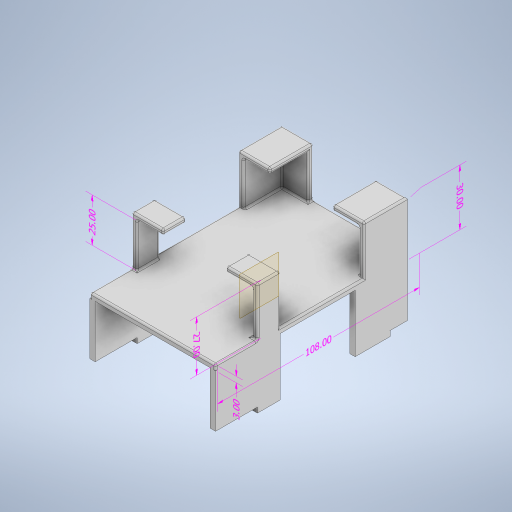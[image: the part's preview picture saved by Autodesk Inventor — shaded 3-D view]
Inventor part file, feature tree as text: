
AUTODESK INVENTOR PART (.ipt)
format: ipt  version: 2023 (Build 270158000, 158)  size: 560,128 bytes
history: native  units: in
note: dims shown in document units (in); Inventor stores cm internally (conversion verified against a paired STEP export)
features: extrude x9, sketch x8, fillet x7, other x6, mirror x3, plane x1
ambient origin geometry x8: Origin, YZ Plane, XZ Plane, XY Plane, X Axis, Y Axis, Z Axis, Center Point
bodies: Solid1 (feature_tree)
feature tree (34):
  other  "Annotations"
  extrude  "BaseBox"  Depth=4.3307in
  extrude  "Extrusion2"  Depth=4.2126in TaperAngle=0.0deg
  extrude  "Extrusion3"  Depth=0.1181in TaperAngle=0.0deg
  extrude  "Extrusion5"  Depth=0.1181in
  extrude  "Extrusion6"  Depth=0.0394in TaperAngle=0.0deg
  fillet  "Fillet1"  Radius=0.0394in
  fillet  "Fillet8"  Radius=0.0394in
  fillet  "Fillet9"  Radius=0.0394in
  fillet  "Fillet10"  Radius=0.0394in
  extrude  "Extrusion7"  Depth=0.1181in
  extrude  "Extrusion8"  Depth=0.1181in
  plane  "Work Plane1"
  extrude  "Extrusion9"  Depth=1.1811in TaperAngle=0.0deg
  fillet  "Fillet13"  Radius=0.1181in
  mirror  "Mirror1"
  fillet  "Fillet14"  [1 undecoded]
  mirror  "Mirror2"
  fillet  "Fillet15"  Radius=0.0394in
  mirror  "Mirror3"
  extrude  "Extrusion10"  Depth=0.0394in
  sketch  "Sketch1"  dims[d0=2.8346in d1=4.3307in]
  sketch  "Sketch2"  dims[d2=1.2205in d3=0.0in d6=4.2126in d7=0.0in]
  sketch  "Sketch4"  dims[d15=0.1181in d16=0.0in d23=0.1181in d24=0.0in]
  sketch  "Sketch7"  dims[d26=0.1181in d27=0.1181in]
  sketch  "Sketch8"  dims[d28=0.1181in d29=1.2205in d30=0.0in d57=0.0394in d64=0.0394in d65=0.0394in d66=0.0394in]
  sketch  "Sketch9"  dims[d67=0.1181in d68=0.1181in]
  sketch  "Sketch11"  dims[d69=4.3307in d70=0.1181in]
  sketch  "Sketch12"  dims[d71=4.3307in d72=1.1811in d73=0.0in d77=0.1181in d78=0.0in d79=0.0in d80=0.0in d85=0.0394in d86=0.0394in d87=0.0394in d91=1.6929in d92=0.0in d93=0.0in d34=0.0in d35=0.3937in d36=4.252in d43=0.0in d44=0.3937in d45=1.1811in d46=0.0in d47=0.3937in d48=1.063in d49=0.0in d50=0.3937in d51=0.1181in d55=0.234in d56=0.9843in]
  other  "Linear Dimension 1"
  other  "Linear Dimension 3"
  other  "Linear Dimension 4"
  other  "Linear Dimension 5"
  other  "Linear Dimension 6"
note: 1 required parameter value undecoded (feature->parameter linkage not recoverable at this tier; creation-order binding heuristic only, values carry confidence <= 0.55)
